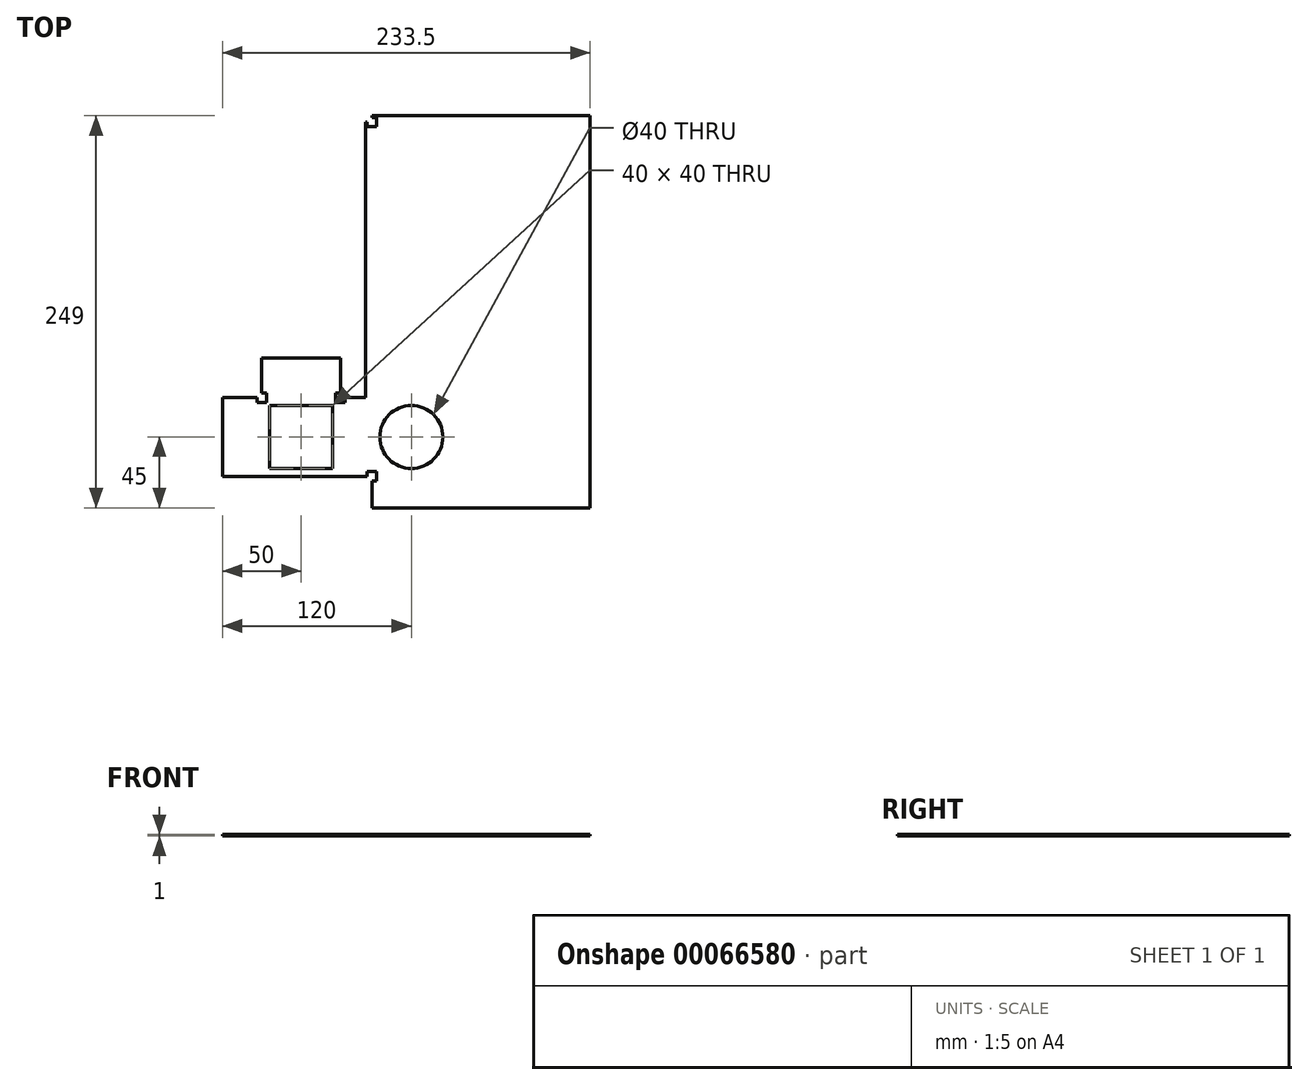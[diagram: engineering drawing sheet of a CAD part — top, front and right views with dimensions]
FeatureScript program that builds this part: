
annotation { "Feature Type Name" : "Feature", "Feature Type Description" : "" }
export const myFeature = defineFeature(function(context is Context, id is Id, definition is map)
    precondition{}
    {
        {
            var Q0;
            Q0=qCreatedBy(makeId("Top.planeOp"),FACE);
            var sketch = newSketch(context, id + "F0", { "sketchPlane" : qUnion([Q0])});
            skLineSegment(sketch, "E0.rect.bottom", {"start": v(0, 112.5) * mm, "end": v(-138.5, 112.5) * mm});
            skLineSegment(sketch, "E0.rect.top", {"start": v(0, -112.5) * mm, "end": v(-138.5, -112.5) * mm});
            skLineSegment(sketch, "E0.rect.right", {"start": v(-138.5, 112.5) * mm, "end": v(-138.5, -112.5) * mm});
            skPoint(sketch, "E0.rect.middle", {"position": v(0, 0) * mm});
            skLineSegment(sketch, "E1.bottom", {"start": v(-128.5, 102.5) * mm, "end": v(0, 102.5) * mm});
            skLineSegment(sketch, "E1.top", {"start": v(-128.5, -44.5) * mm, "end": v(0, -44.5) * mm});
            skLineSegment(sketch, "E1.left", {"start": v(-128.5, 102.5) * mm, "end": v(-128.5, -44.5) * mm});
            skCircle(sketch, "E2", {"center": v(-113.5, -87.5) * mm, "radius": 20 * mm});
            skLineSegment(sketch, "E3", {"start": v(0, 112.5) * mm, "end": v(0, -112.5) * mm});
            skLineSegment(sketch, "E4.bottom", {"start": v(-138.5, -112.5) * mm, "end": v(-158.5, -112.5) * mm});
            skLineSegment(sketch, "E4.top", {"start": v(-138.5, -62.5) * mm, "end": v(-158.5, -62.5) * mm});
            skLineSegment(sketch, "E4.left", {"start": v(-138.5, -112.5) * mm, "end": v(-138.5, -62.5) * mm});
            skLineSegment(sketch, "E4.right", {"start": v(-158.5, -112.5) * mm, "end": v(-158.5, -62.5) * mm});
            skLineSegment(sketch, "E5.bottom", {"start": v(-158.5, -62.5) * mm, "end": v(-208.5, -62.5) * mm});
            skLineSegment(sketch, "E5.top", {"start": v(-158.5, -112.5) * mm, "end": v(-208.5, -112.5) * mm});
            skLineSegment(sketch, "E5.left", {"start": v(-158.5, -62.5) * mm, "end": v(-158.5, -112.5) * mm});
            skLineSegment(sketch, "E5.right", {"start": v(-208.5, -62.5) * mm, "end": v(-208.5, -112.5) * mm});
            skLineSegment(sketch, "E6.bottom", {"start": v(-208.5, -62.5) * mm, "end": v(-228.5, -62.5) * mm});
            skLineSegment(sketch, "E6.top", {"start": v(-208.5, -112.5) * mm, "end": v(-228.5, -112.5) * mm});
            skLineSegment(sketch, "E6.right", {"start": v(-228.5, -62.5) * mm, "end": v(-228.5, -112.5) * mm});
            skLineSegment(sketch, "E7.bottom", {"start": v(-208.5, -62.5) * mm, "end": v(-158.5, -62.5) * mm});
            skLineSegment(sketch, "E7.top", {"start": v(-208.5, -42.5) * mm, "end": v(-158.5, -42.5) * mm});
            skLineSegment(sketch, "E7.left", {"start": v(-208.5, -62.5) * mm, "end": v(-208.5, -42.5) * mm});
            skLineSegment(sketch, "E7.right", {"start": v(-158.5, -62.5) * mm, "end": v(-158.5, -42.5) * mm});
            skLineSegment(sketch, "E8.bottom", {"start": v(-228.5, -62.5) * mm, "end": v(-233.5, -62.5) * mm});
            skLineSegment(sketch, "E8.top", {"start": v(-228.5, -112.5) * mm, "end": v(-233.5, -112.5) * mm});
            skLineSegment(sketch, "E8.right", {"start": v(-233.5, -62.5) * mm, "end": v(-233.5, -112.5) * mm});
            skLineSegment(sketch, "E9.bottom", {"start": v(-203.5, -67.5) * mm, "end": v(-163.5, -67.5) * mm});
            skLineSegment(sketch, "E9.top", {"start": v(-203.5, -107.5) * mm, "end": v(-163.5, -107.5) * mm});
            skLineSegment(sketch, "E9.left", {"start": v(-203.5, -67.5) * mm, "end": v(-203.5, -107.5) * mm});
            skLineSegment(sketch, "E9.right", {"start": v(-163.5, -67.5) * mm, "end": v(-163.5, -107.5) * mm});
            skLineSegment(sketch, "E10.bottom", {"start": v(-138.5, -62.5) * mm, "end": v(-142.5, -62.5) * mm});
            skLineSegment(sketch, "E10.top", {"start": v(-138.5, 112.5) * mm, "end": v(-142.5, 112.5) * mm});
            skLineSegment(sketch, "E10.left", {"start": v(-138.5, -62.5) * mm, "end": v(-138.5, 112.5) * mm});
            skLineSegment(sketch, "E10.right", {"start": v(-142.5, -62.5) * mm, "end": v(-142.5, 112.5) * mm});
            skLineSegment(sketch, "E11.bottom", {"start": v(-138.5, -112.5) * mm, "end": v(0, -112.5) * mm});
            skLineSegment(sketch, "E11.top", {"start": v(-138.5, -132.5) * mm, "end": v(0, -132.5) * mm});
            skLineSegment(sketch, "E11.left", {"start": v(-138.5, -112.5) * mm, "end": v(-138.5, -132.5) * mm});
            skLineSegment(sketch, "E11.right", {"start": v(0, -112.5) * mm, "end": v(0, -132.5) * mm});
            skLineSegment(sketch, "E12", {"start": v(0, -112.5) * mm, "end": v(0, 112.5) * mm});
            skLineSegment(sketch, "E13.top", {"start": v(-208.5, -37.5) * mm, "end": v(-158.5, -37.5) * mm});
            skLineSegment(sketch, "E13.left", {"start": v(-208.5, -42.5) * mm, "end": v(-208.5, -37.5) * mm});
            skLineSegment(sketch, "E13.right", {"start": v(-158.5, -42.5) * mm, "end": v(-158.5, -37.5) * mm});
            skLineSegment(sketch, "E14.bottom", {"start": v(-138.5, 112.5) * mm, "end": v(0, 112.5) * mm});
            skLineSegment(sketch, "E14.top", {"start": v(-138.5, 116.5) * mm, "end": v(0, 116.5) * mm});
            skLineSegment(sketch, "E14.left", {"start": v(-138.5, 112.5) * mm, "end": v(-138.5, 116.5) * mm});
            skLineSegment(sketch, "E14.right", {"start": v(0, 112.5) * mm, "end": v(0, 116.5) * mm});
            skSolve(sketch);
        }
        {
            var Q0;
            Q0=makeQuery(id+"F0.imprint","IMPRINT",FACE,{"disambiguationData":[TD([[makeQuery(id+"F0.imprint","IMPRINT",EDGE,{"derivedFrom":sQuery(id+"F0.wireOp",EDGE,"E8.bottom")}),1.0]])]});
            var Q1;
            Q1=makeQuery(id+"F0.imprint","IMPRINT",FACE,{"disambiguationData":[TD([[makeQuery(id+"F0.imprint","IMPRINT",EDGE,{"derivedFrom":sQuery(id+"F0.wireOp",EDGE,"E11.bottom")}),-1.0]])]});
            var Q2;
            Q2=makeQuery(id+"F0.imprint","IMPRINT",FACE,{"disambiguationData":[TD([[makeQuery(id+"F0.imprint","IMPRINT",EDGE,{"derivedFrom":sQuery(id+"F0.wireOp",EDGE,"E7.top")}),1.0]])]});
            var Q3;
            Q3=makeQuery(id+"F0.imprint","IMPRINT",FACE,{"disambiguationData":[TD([[makeQuery(id+"F0.imprint","IMPRINT",EDGE,{"derivedFrom":sQuery(id+"F0.wireOp",EDGE,"E14.bottom")}),1.0]])]});
            var Q4;
            Q4=makeQuery(id+"F0.imprint","IMPRINT",FACE,{"disambiguationData":[TD([[makeQuery(id+"F0.imprint","IMPRINT",EDGE,{"derivedFrom":sQuery(id+"F0.wireOp",EDGE,"E6.bottom")}),1.0]])]});
            var Q5;
            Q5=makeQuery(id+"F0.imprint","IMPRINT",FACE,{"disambiguationData":[TD([[makeQuery(id+"F0.imprint","IMPRINT",EDGE,{"derivedFrom":sQuery(id+"F0.wireOp",EDGE,"E7.bottom")}),1.0]])]});
            var Q6;
            Q6=makeQuery(id+"F0.imprint","IMPRINT",FACE,{"disambiguationData":[TD([[makeQuery(id+"F0.imprint","IMPRINT",EDGE,{"derivedFrom":sQuery(id+"F0.wireOp",EDGE,"E10.bottom")}),-1.0]])]});
            var Q7;
            Q7=makeQuery(id+"F0.imprint","IMPRINT",FACE,{"disambiguationData":[TD([[makeQuery(id+"F0.imprint","IMPRINT",EDGE,{"derivedFrom":sQuery(id+"F0.wireOp",EDGE,"E4.bottom")}),-1.0]])]});
            var Q8;
            Q8=makeQuery(id+"F0.imprint","IMPRINT",FACE,{"disambiguationData":[TD([[makeQuery(id+"F0.imprint","IMPRINT",EDGE,{"derivedFrom":sQuery(id+"F0.wireOp",EDGE,"E5.top")}),-1.0]])]});
            var Q9;
            {var subQ1=sQuery(id+"F0.wireOp",EDGE,"E1.bottom");Q9=makeQuery(id+"F0.imprint","IMPRINT",FACE,{"disambiguationData":[TD([[makeQuery(id+"F0.imprint","IMPRINT",EDGE,{"derivedFrom":subQ1}),1.0]])]});}
            extrude(context, id + "F1", {"entities" : qUnion([Q0, Q1, Q2, Q3, Q4, Q5, Q6, Q7, Q8, Q9]), "depth" : 1 * mm});
        }
        {
            var Q0;
            Q0 = qSketchRegion(id + "F0", true);
            extrude(context, id + "F2", {"entities" : qUnion([Q0]), "operationType" : NewBodyOperationType.ADD, "depth" : 1 * mm});
        }
        {
            var Q0;
            {var subQ0=sQuery(id+"F0.wireOp",EDGE,"E14.right");var subQ1=sQuery(id+"F0.wireOp",EDGE,"E14.left");var subQ2=sQuery(id+"F0.wireOp",EDGE,"E14.top");var subQ3=sQuery(id+"F0.wireOp",EDGE,"E13.right");var subQ4=sQuery(id+"F0.wireOp",EDGE,"E13.left");var subQ5=sQuery(id+"F0.wireOp",EDGE,"E13.top");var subQ6=sQuery(id+"F0.wireOp",EDGE,"E12");var subQ7=sQuery(id+"F0.wireOp",EDGE,"E11.right");var subQ8=sQuery(id+"F0.wireOp",EDGE,"E11.left");var subQ9=sQuery(id+"F0.wireOp",EDGE,"E11.top");var subQ10=sQuery(id+"F0.wireOp",EDGE,"E10.right");var subQ11=sQuery(id+"F0.wireOp",EDGE,"E10.top");var subQ12=sQuery(id+"F0.wireOp",EDGE,"E9.right");var subQ13=sQuery(id+"F0.wireOp",EDGE,"E9.left");var subQ14=sQuery(id+"F0.wireOp",EDGE,"E9.top");var subQ15=sQuery(id+"F0.wireOp",EDGE,"E9.bottom");var subQ16=sQuery(id+"F0.wireOp",EDGE,"E8.right");var subQ17=sQuery(id+"F0.wireOp",EDGE,"E8.top");var subQ18=sQuery(id+"F0.wireOp",EDGE,"E8.bottom");var subQ19=sQuery(id+"F0.wireOp",EDGE,"E7.right");var subQ20=sQuery(id+"F0.wireOp",EDGE,"E7.left");var subQ21=sQuery(id+"F0.wireOp",EDGE,"E6.top");var subQ22=sQuery(id+"F0.wireOp",EDGE,"E6.bottom");var subQ23=sQuery(id+"F0.wireOp",EDGE,"E5.top");var subQ24=sQuery(id+"F0.wireOp",EDGE,"E4.top");var subQ25=sQuery(id+"F0.wireOp",EDGE,"E4.bottom");var subQ26=sQuery(id+"F0.wireOp",EDGE,"E2");Q0=makeQuery(id+"F2.boolean.opBoolean","MERGE",FACE,{"derivedFrom":[makeQuery(id+"F1.opExtrude","CAP_FACE",FACE,{"disambiguationData":[OSD([sQuery(id+"F0.wireOp",EDGE,"E1.bottom"),sQuery(id+"F0.wireOp",EDGE,"E1.top"),sQuery(id+"F0.wireOp",EDGE,"E1.left"),subQ26,subQ25,subQ24,subQ23,subQ22,subQ21,subQ20,subQ19,subQ18,subQ17,subQ16,subQ15,subQ14,subQ13,subQ12,subQ11,subQ10,subQ9,subQ8,subQ7,subQ6,subQ5,subQ4,subQ3,subQ2,subQ1,subQ0])],"isStart":false}),makeQuery(id+"F2.opExtrude","CAP_FACE",FACE,{"disambiguationData":[OSD([subQ26,subQ25,subQ24,subQ23,subQ22,subQ21,subQ20,subQ19,subQ18,subQ17,subQ16,subQ15,subQ14,subQ13,subQ12,subQ11,subQ10,subQ9,subQ8,subQ7,subQ6,subQ5,subQ4,subQ3,subQ2,subQ1,subQ0])],"isStart":false})]});}
            var sketch = newSketch(context, id + "F3", { "sketchPlane" : qUnion([Q0])});
            skLineSegment(sketch, "E15.rect.bottom", {"start": v(-135.5, -109.5) * mm, "end": v(-141.5, -109.5) * mm});
            skLineSegment(sketch, "E15.rect.top", {"start": v(-135.5, -115.5) * mm, "end": v(-141.5, -115.5) * mm});
            skLineSegment(sketch, "E15.rect.left", {"start": v(-135.5, -109.5) * mm, "end": v(-135.5, -115.5) * mm});
            skLineSegment(sketch, "E15.rect.right", {"start": v(-141.5, -109.5) * mm, "end": v(-141.5, -115.5) * mm});
            skPoint(sketch, "E15.rect.middle", {"position": v(-138.5, -112.5) * mm});
            skLineSegment(sketch, "E16.rect.bottom", {"start": v(-155.5, -59.5) * mm, "end": v(-161.5, -59.5) * mm});
            skLineSegment(sketch, "E16.rect.top", {"start": v(-155.5, -65.5) * mm, "end": v(-161.5, -65.5) * mm});
            skLineSegment(sketch, "E16.rect.left", {"start": v(-155.5, -59.5) * mm, "end": v(-155.5, -65.5) * mm});
            skLineSegment(sketch, "E16.rect.right", {"start": v(-161.5, -59.5) * mm, "end": v(-161.5, -65.5) * mm});
            skPoint(sketch, "E16.rect.middle", {"position": v(-158.5, -62.5) * mm});
            skLineSegment(sketch, "E17.rect.bottom", {"start": v(-205.5, -59.5) * mm, "end": v(-211.5, -59.5) * mm});
            skLineSegment(sketch, "E17.rect.top", {"start": v(-205.5, -65.5) * mm, "end": v(-211.5, -65.5) * mm});
            skLineSegment(sketch, "E17.rect.left", {"start": v(-205.5, -59.5) * mm, "end": v(-205.5, -65.5) * mm});
            skLineSegment(sketch, "E17.rect.right", {"start": v(-211.5, -59.5) * mm, "end": v(-211.5, -65.5) * mm});
            skPoint(sketch, "E17.rect.middle", {"position": v(-208.5, -62.5) * mm});
            skLineSegment(sketch, "E18.rect.bottom", {"start": v(-135.5, 115.5) * mm, "end": v(-141.5, 115.5) * mm});
            skLineSegment(sketch, "E18.rect.top", {"start": v(-135.5, 109.5) * mm, "end": v(-141.5, 109.5) * mm});
            skLineSegment(sketch, "E18.rect.left", {"start": v(-135.5, 115.5) * mm, "end": v(-135.5, 109.5) * mm});
            skLineSegment(sketch, "E18.rect.right", {"start": v(-141.5, 115.5) * mm, "end": v(-141.5, 109.5) * mm});
            skPoint(sketch, "E18.rect.middle", {"position": v(-138.5, 112.5) * mm});
            skSolve(sketch);
        }
        {
            var Q0;
            Q0 = qSketchRegion(id + "F3", true);
            extrude(context, id + "F4", {"entities" : qUnion([Q0]), "operationType" : NewBodyOperationType.REMOVE, "oppositeDirection" : true, "depth" : 25 * mm});
        }
    });
